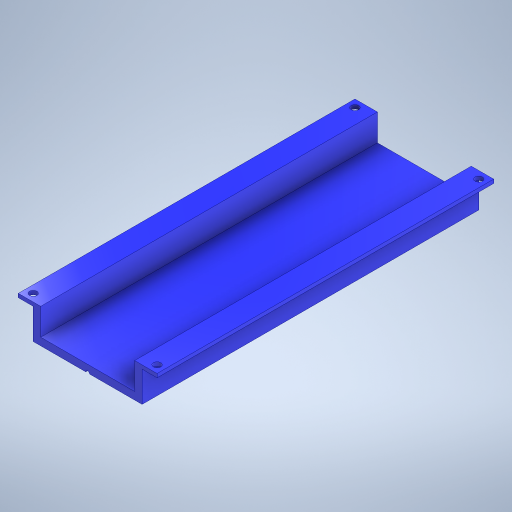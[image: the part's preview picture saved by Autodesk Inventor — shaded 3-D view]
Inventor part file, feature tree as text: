
AUTODESK INVENTOR PART (.ipt)
format: ipt  version: 2023 (Build 270158000, 158)  size: 305,664 bytes
history: native  units: mm
features: extrude x2, sketch x2
ambient origin geometry x8: Origin, YZ Plane, XZ Plane, XY Plane, X Axis, Y Axis, Z Axis, Center Point
bodies: Solid1 (feature_tree)
feature tree (4):
  extrude  "Extrusion1"  Depth=35.75mm
  extrude  "Extrusion2"  Depth=450.0mm TaperAngle=0.0deg
  sketch  "Sketch1"  dims[d0=10.0mm d1=35.75mm]
  sketch  "Sketch2"  dims[d2=10.0mm d3=450.0mm d4=0.0mm d5=20.0mm d6=10.0mm d7=20.0mm d8=20.0mm d9=20.0mm d10=20.0mm d11=20.0mm d12=20.0mm d13=10.0mm d14=10.0mm d15=10.0mm d16=450.0mm d17=0.0mm]
